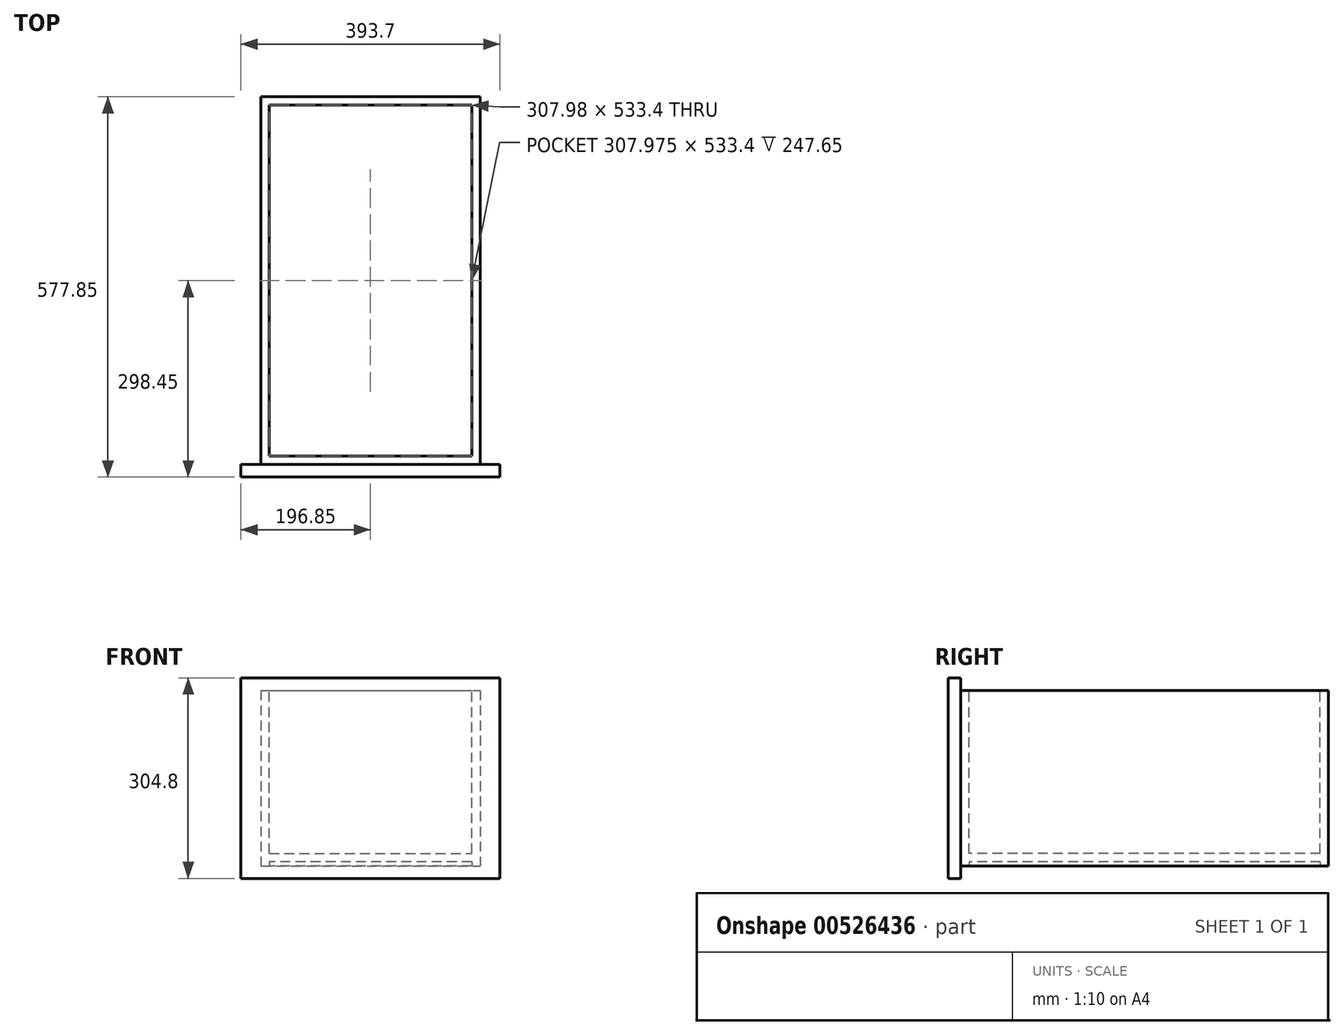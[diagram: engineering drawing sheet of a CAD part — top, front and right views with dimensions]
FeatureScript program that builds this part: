
annotation { "Feature Type Name" : "Feature", "Feature Type Description" : "" }
export const myFeature = defineFeature(function(context is Context, id is Id, definition is map)
    precondition{}
    {
        {
            var Q0;
            Q0=qCreatedBy(makeId("Front.planeOp"),FACE);
            var sketch = newSketch(context, id + "F0", { "sketchPlane" : qUnion([Q0])});
            skLineSegment(sketch, "E0.bottom", {"start": v(196.85, 152.4) * mm, "end": v(-196.85, 152.4) * mm});
            skLineSegment(sketch, "E0.top", {"start": v(196.85, -152.4) * mm, "end": v(-196.85, -152.4) * mm});
            skLineSegment(sketch, "E0.left", {"start": v(196.85, 152.4) * mm, "end": v(196.85, -152.4) * mm});
            skLineSegment(sketch, "E0.right", {"start": v(-196.85, 152.4) * mm, "end": v(-196.85, -152.4) * mm});
            skPoint(sketch, "E0.middle", {"position": v(0, 0) * mm});
            skSolve(sketch);
        }
        {
            var Q0;
            Q0=makeQuery(id+"F0.imprint","IMPRINT",FACE,{"disambiguationData":[TD([[makeQuery(id+"F0.imprint","IMPRINT",EDGE,{"derivedFrom":sQuery(id+"F0.wireOp",EDGE,"E0.bottom")}),1.0]])]});
            extrude(context, id + "F1", {"entities" : qUnion([Q0]), "depth" : 19.05 * mm, "offsetDistance" : 25.4 * mm});
        }
        {
            var Q0;
            Q0=makeQuery(id+"F1.opExtrude","CAP_FACE",FACE,{"disambiguationData":[OSD([sQuery(id+"F0.wireOp",EDGE,"E0.bottom"),sQuery(id+"F0.wireOp",EDGE,"E0.top"),sQuery(id+"F0.wireOp",EDGE,"E0.left"),sQuery(id+"F0.wireOp",EDGE,"E0.right")])],"isStart":true});
            var sketch = newSketch(context, id + "F2", { "sketchPlane" : qUnion([Q0])});
            skLineSegment(sketch, "E1.bottom", {"start": v(166.69, 133.35) * mm, "end": v(-166.69, 133.35) * mm});
            skLineSegment(sketch, "E1.top", {"start": v(166.69, -133.35) * mm, "end": v(-166.69, -133.35) * mm});
            skLineSegment(sketch, "E1.left", {"start": v(166.69, 133.35) * mm, "end": v(166.69, -133.35) * mm});
            skLineSegment(sketch, "E1.right", {"start": v(-166.69, 133.35) * mm, "end": v(-166.69, -133.35) * mm});
            skPoint(sketch, "E1.middle", {"position": v(0, 0) * mm});
            skSolve(sketch);
        }
        {
            var Q0;
            Q0=makeQuery(id+"F2.imprint","IMPRINT",FACE,{"disambiguationData":[TD([[makeQuery(id+"F2.imprint","IMPRINT",EDGE,{"derivedFrom":sQuery(id+"F2.wireOp",EDGE,"E1.bottom")}),1.0]])]});
            extrude(context, id + "F3", {"entities" : qUnion([Q0]), "operationType" : NewBodyOperationType.ADD, "depth" : 558.8 * mm, "offsetDistance" : 25.4 * mm});
        }
        {
            var Q0;
            Q0=makeQuery(id+"F3.opExtrude","SWEPT_FACE",FACE,{"disambiguationData":[OSD([sQuery(id+"F2.wireOp",EDGE,"E1.bottom")])]});
            var sketch = newSketch(context, id + "F4", { "sketchPlane" : qUnion([Q0])});
            skLineSegment(sketch, "E2", {"start": v(-166.69, 558.8) * mm, "end": v(-153.99, 558.8) * mm});
            skLineSegment(sketch, "E3", {"start": v(-153.99, 558.8) * mm, "end": v(-153.99, 546.1) * mm});
            skLineSegment(sketch, "E4.bottom", {"start": v(-153.99, 546.1) * mm, "end": v(153.99, 546.1) * mm});
            skLineSegment(sketch, "E4.top", {"start": v(-153.99, 12.7) * mm, "end": v(153.99, 12.7) * mm});
            skLineSegment(sketch, "E4.left", {"start": v(-153.99, 546.1) * mm, "end": v(-153.99, 12.7) * mm});
            skLineSegment(sketch, "E4.right", {"start": v(153.99, 546.1) * mm, "end": v(153.99, 12.7) * mm});
            skSolve(sketch);
        }
        {
            var Q0;
            Q0=makeQuery(id+"F4.imprint","IMPRINT",FACE,{"disambiguationData":[TD([[makeQuery(id+"F4.imprint","IMPRINT",EDGE,{"derivedFrom":sQuery(id+"F4.wireOp",EDGE,"E4.bottom")}),-1.0]])]});
            extrude(context, id + "F5", {"entities" : qUnion([Q0]), "operationType" : NewBodyOperationType.REMOVE, "oppositeDirection" : true, "depth" : 247.65 * mm, "offsetDistance" : 25.4 * mm});
        }
        {
            var Q0;
            Q0=makeQuery(id+"F3.opExtrude","SWEPT_FACE",FACE,{"disambiguationData":[OSD([sQuery(id+"F2.wireOp",EDGE,"E1.top")])]});
            var sketch = newSketch(context, id + "F6", { "sketchPlane" : qUnion([Q0])});
            skLineSegment(sketch, "E5", {"start": v(166.69, -558.8) * mm, "end": v(153.99, -558.8) * mm});
            skLineSegment(sketch, "E6", {"start": v(153.99, -558.8) * mm, "end": v(153.99, -546.1) * mm});
            skLineSegment(sketch, "E7.bottom", {"start": v(153.99, -546.1) * mm, "end": v(-153.99, -546.1) * mm});
            skLineSegment(sketch, "E7.top", {"start": v(153.99, -12.7) * mm, "end": v(-153.99, -12.7) * mm});
            skLineSegment(sketch, "E7.left", {"start": v(153.99, -546.1) * mm, "end": v(153.99, -12.7) * mm});
            skLineSegment(sketch, "E7.right", {"start": v(-153.99, -546.1) * mm, "end": v(-153.99, -12.7) * mm});
            skSolve(sketch);
        }
        {
            var Q0;
            Q0=makeQuery(id+"F6.imprint","IMPRINT",FACE,{"disambiguationData":[TD([[makeQuery(id+"F6.imprint","IMPRINT",EDGE,{"derivedFrom":sQuery(id+"F6.wireOp",EDGE,"E7.bottom")}),-1.0]])]});
            extrude(context, id + "F7", {"entities" : qUnion([Q0]), "operationType" : NewBodyOperationType.REMOVE, "oppositeDirection" : true, "depth" : 6.35 * mm, "offsetDistance" : 25.4 * mm});
        }
    });
